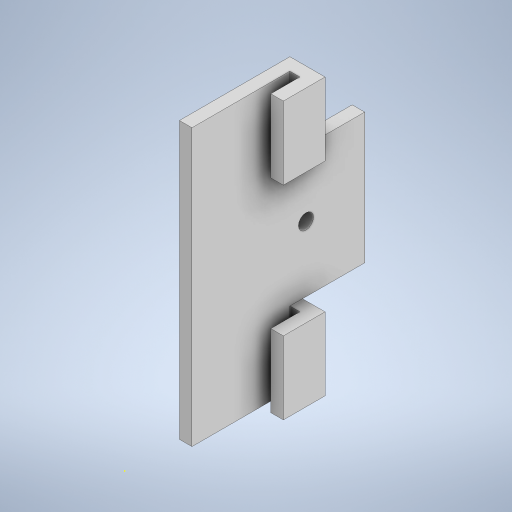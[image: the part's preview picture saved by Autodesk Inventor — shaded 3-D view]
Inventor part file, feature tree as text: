
AUTODESK INVENTOR PART (.ipt)
format: ipt  version: 2024.3 (Build 283343000, 343)  size: 319,488 bytes
history: native  units: in
note: dims shown in document units (in); Inventor stores cm internally (conversion verified against a paired STEP export)
features: sketch x8, extrude x7
ambient origin geometry x8: Origin, YZ Plane, XZ Plane, XY Plane, X Axis, Y Axis, Z Axis, Center Point
bodies: Solid1 (feature_tree)
feature tree (15):
  extrude  "Extrusion1"  Depth=0.2677in
  extrude  "Extrusion2"  Depth=0.0984in
  extrude  "Extrusion3"  Depth=0.2283in
  extrude  "Extrusion4"  Depth=0.2283in
  extrude  "Extrusion5"  Depth=0.5709in
  sketch  "Sketch6"  dims[d11=1.5551in d12=1.0236in d13=0.0in]
  extrude  "Extrusion6"  Depth=1.0236in TaperAngle=0.0deg
  extrude  "Extrusion7"  Depth=0.5709in
  sketch  "Sketch1"  dims[d0=2.1339in d1=0.2677in]
  sketch  "Sketch2"  dims[d2=0.3268in d3=0.0984in]
  sketch  "Sketch3"  dims[d4=0.2283in d5=0.0709in]
  sketch  "Sketch4"  dims[d6=0.3268in d7=0.2283in]
  sketch  "Sketch5"  dims[d8=0.5709in d9=0.0in d10=1.5551in]
  sketch  "Sketch7"  dims[d14=0.5709in d15=0.0in d18=0.5276in]
  sketch  "Sketch8"  dims[d19=0.1181in d20=0.1772in d21=0.0in d22=0.2283in d23=0.2283in d24=2.4562in d25=0.0in d26=2.4562in d27=0.0in d28=0.0276in d29=0.0in]
